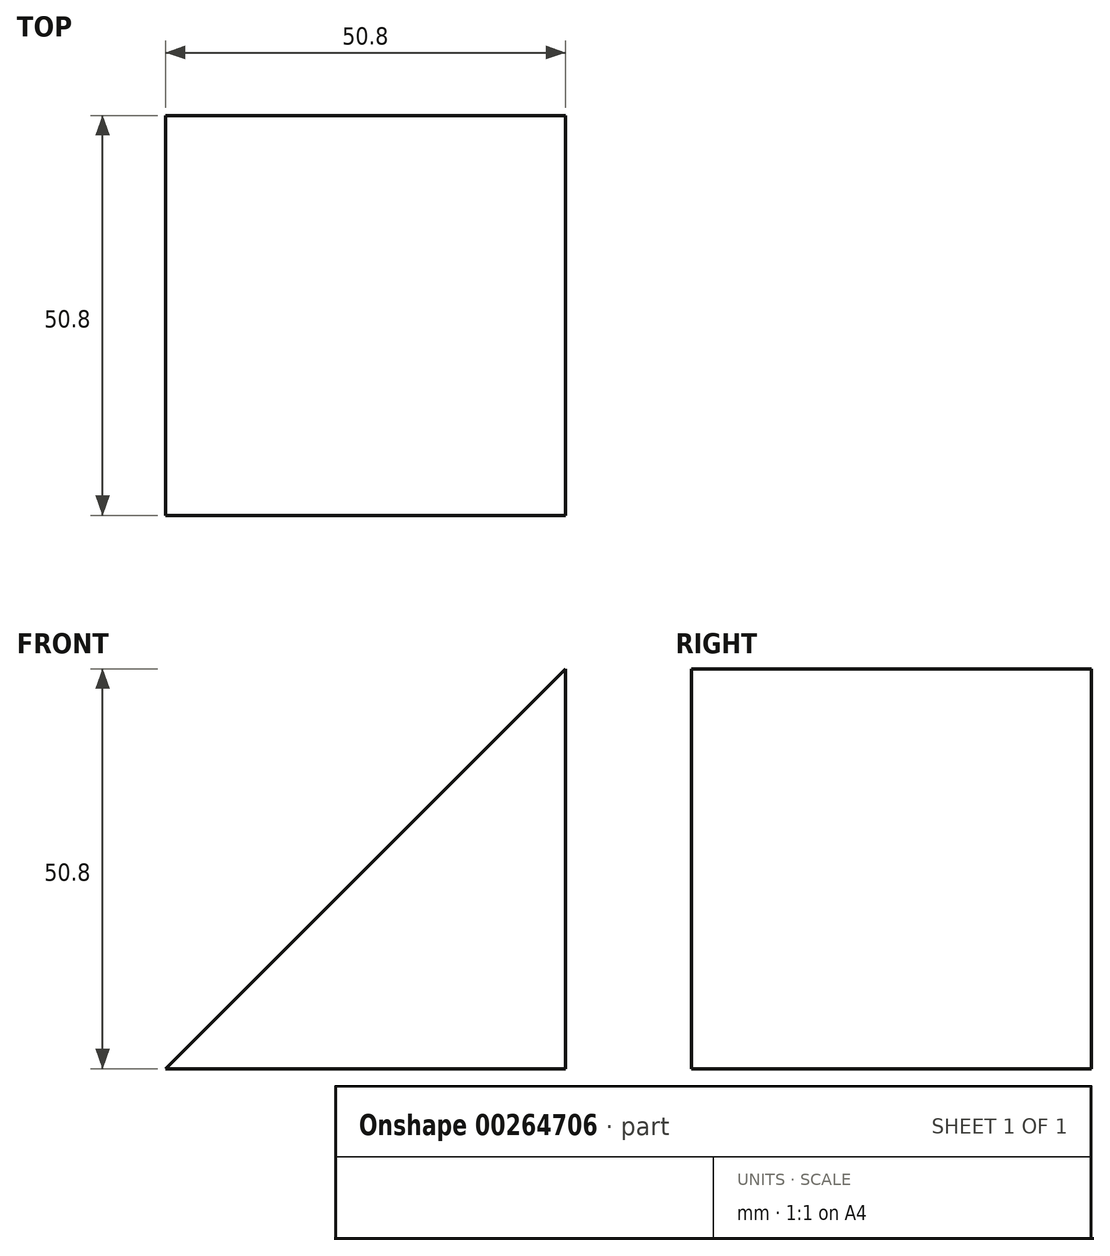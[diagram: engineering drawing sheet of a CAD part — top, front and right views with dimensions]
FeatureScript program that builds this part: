
annotation { "Feature Type Name" : "Feature", "Feature Type Description" : "" }
export const myFeature = defineFeature(function(context is Context, id is Id, definition is map)
    precondition{}
    {
        {
            var Q0;
            Q0=qCreatedBy(makeId("Front.planeOp"),FACE);
            var sketch = newSketch(context, id + "F0", { "sketchPlane" : qUnion([Q0])});
            skLineSegment(sketch, "E0", {"start": v(0, 0) * mm, "end": v(-50.8, 0) * mm});
            skLineSegment(sketch, "E1", {"start": v(0, 0) * mm, "end": v(0, 50.8) * mm});
            skLineSegment(sketch, "E2", {"start": v(0, 50.8) * mm, "end": v(-50.8, 0) * mm});
            skSolve(sketch);
        }
        {
            var Q0;
            Q0 = qSketchRegion(id + "F0", true);
            extrude(context, id + "F1", {"entities" : qUnion([Q0]), "depth" : 50.8 * mm});
        }
    });
